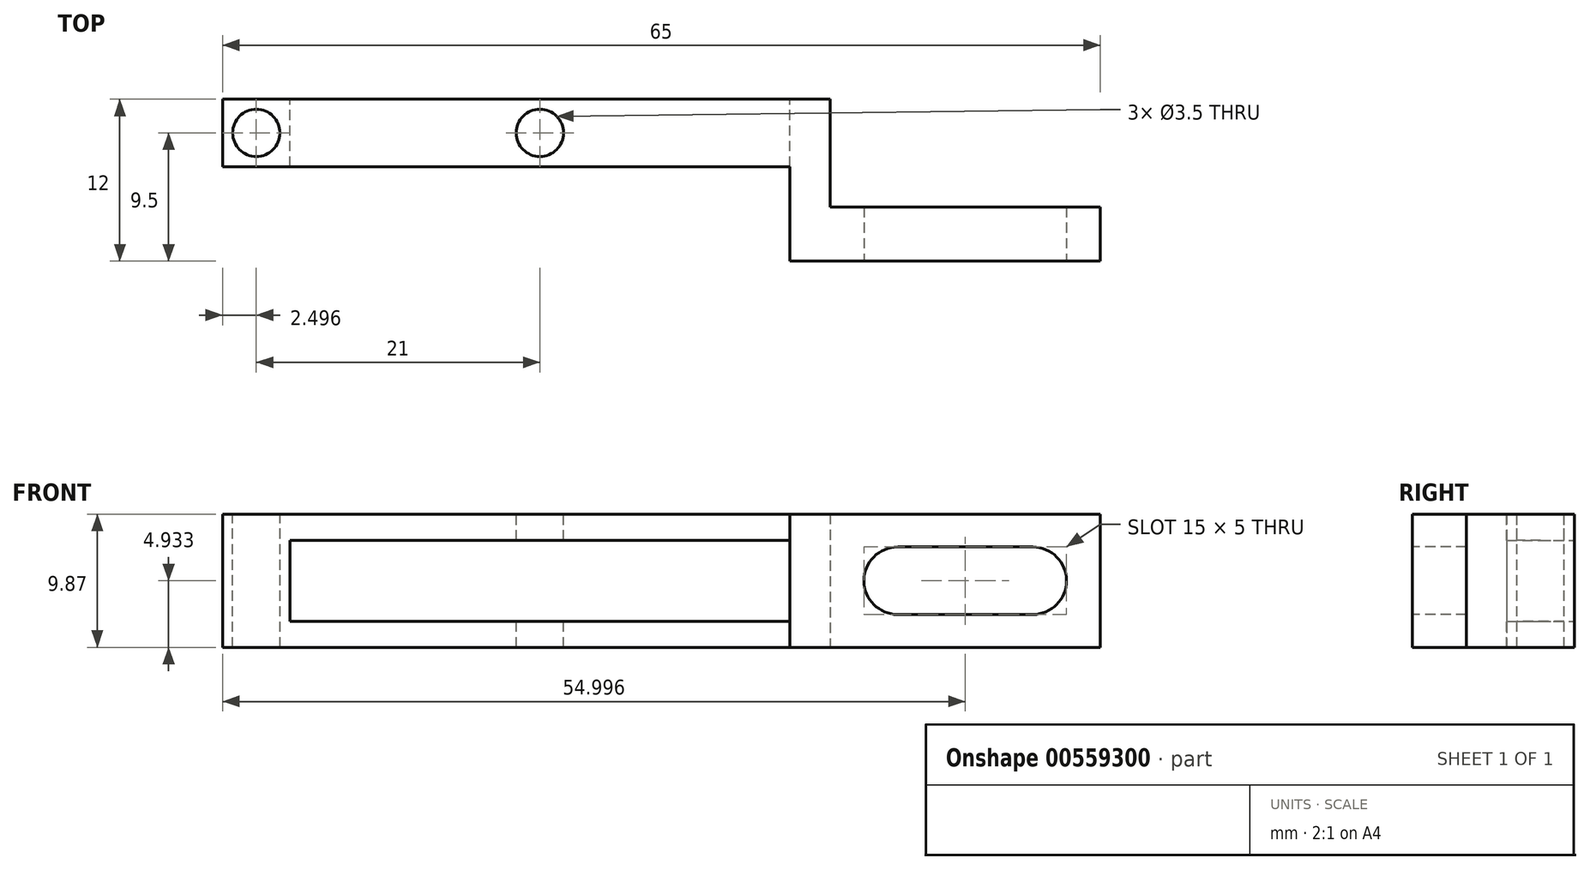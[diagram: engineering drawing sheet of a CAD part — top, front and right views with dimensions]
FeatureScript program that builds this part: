
annotation { "Feature Type Name" : "Feature", "Feature Type Description" : "" }
export const myFeature = defineFeature(function(context is Context, id is Id, definition is map)
    precondition{}
    {
        {
            var Q0;
            Q0=qCreatedBy(makeId("Front.planeOp"),FACE);
            var sketch = newSketch(context, id + "F0", { "sketchPlane" : qUnion([Q0])});
            skLineSegment(sketch, "E0.top", {"start": v(-18.46, -6.81) * mm, "end": v(26.54, -6.81) * mm});
            skLineSegment(sketch, "E0.left", {"start": v(-18.46, 3.06) * mm, "end": v(-18.46, -6.81) * mm});
            skLineSegment(sketch, "E1", {"start": v(-18.46, -1.88) * mm, "end": v(-1.71, -1.88) * mm, "construction": true});
            skLineSegment(sketch, "E2", {"start": v(-1.71, -1.88) * mm, "end": v(-1.71, -4.88) * mm, "construction": true});
            skLineSegment(sketch, "E3", {"start": v(-13.46, -4.88) * mm, "end": v(26.54, -4.88) * mm});
            skLineSegment(sketch, "E4", {"start": v(26.54, -4.88) * mm, "end": v(26.54, -6.81) * mm});
            skLineSegment(sketch, "E5", {"start": v(-18.46, 3.06) * mm, "end": v(26.54, 3.06) * mm});
            skLineSegment(sketch, "E6", {"start": v(-1.71, -1.88) * mm, "end": v(-1.71, 1.12) * mm});
            skLineSegment(sketch, "E7", {"start": v(26.54, 3.06) * mm, "end": v(26.54, 1.12) * mm});
            skLineSegment(sketch, "E8", {"start": v(26.54, 1.12) * mm, "end": v(-13.46, 1.12) * mm});
            skLineSegment(sketch, "E9", {"start": v(-13.46, 1.12) * mm, "end": v(-13.46, -4.88) * mm});
            skLineSegment(sketch, "E10", {"start": v(-13.46, -4.88) * mm, "end": v(-18.46, -4.88) * mm});
            skLineSegment(sketch, "E11", {"start": v(26.54, -4.88) * mm, "end": v(26.54, 1.12) * mm});
            skLineSegment(sketch, "E12", {"start": v(23.54, -4.88) * mm, "end": v(23.54, 1.12) * mm});
            skLineSegment(sketch, "E13", {"start": v(23.54, 1.12) * mm, "end": v(23.54, -1.88) * mm});
            skLineSegment(sketch, "E14", {"start": v(23.54, -1.88) * mm, "end": v(26.54, -1.88) * mm});
            skSolve(sketch);
        }
        {
            var Q0;
            Q0 = qSketchRegion(id + "F0", true);
            extrude(context, id + "F1", {"entities" : qUnion([Q0]), "depth" : 5 * mm, "offsetDistance" : 25 * mm});
        }
        {
            var Q0;
            Q0=makeQuery(id+"F1.opExtrude","SWEPT_FACE",FACE,{"disambiguationData":[OSD([sQuery(id+"F0.wireOp",EDGE,"E5")])]});
            var sketch = newSketch(context, id + "F2", { "sketchPlane" : qUnion([Q0])});
            skLineSegment(sketch, "E15", {"start": v(-18.46, 0) * mm, "end": v(-18.46, -5) * mm});
            skLineSegment(sketch, "E16", {"start": v(-18.46, -2.5) * mm, "end": v(-15.96, -2.5) * mm});
            skCircle(sketch, "E17", {"center": v(-15.96, -2.5) * mm, "radius": 1.75 * mm});
            skLineSegment(sketch, "E18", {"start": v(4.04, 0) * mm, "end": v(4.04, -2.5) * mm});
            skLineSegment(sketch, "E19", {"start": v(4.04, -2.5) * mm, "end": v(5.04, -2.5) * mm});
            skCircle(sketch, "E20", {"center": v(5.04, -2.5) * mm, "radius": 1.75 * mm});
            skCircle(sketch, "E21", {"center": v(5.04, -2.5) * mm, "radius": 10 * mm});
            skSolve(sketch);
        }
        {
            var Q0;
            Q0=makeQuery(id+"F2.imprint","IMPRINT",FACE,{"disambiguationData":[TD([[makeQuery(id+"F2.imprint","IMPRINT",EDGE,{"derivedFrom":sQuery(id+"F2.wireOp",EDGE,"E17")}),1.0]])]});
            var Q1;
            Q1=makeQuery(id+"F2.imprint","IMPRINT",FACE,{"disambiguationData":[TD([[makeQuery(id+"F2.imprint","IMPRINT",EDGE,{"derivedFrom":sQuery(id+"F2.wireOp",EDGE,"E20")}),1.0]])]});
            extrude(context, id + "F3", {"entities" : qUnion([Q0, Q1]), "operationType" : NewBodyOperationType.REMOVE, "oppositeDirection" : true, "depth" : 25 * mm, "offsetDistance" : 25 * mm});
        }
        {
            var Q0;
            Q0=makeQuery(id+"F1.opExtrude","CAP_FACE",FACE,{"disambiguationData":[OSD([sQuery(id+"F0.wireOp",EDGE,"E0.top"),sQuery(id+"F0.wireOp",EDGE,"E0.left"),sQuery(id+"F0.wireOp",EDGE,"E3"),sQuery(id+"F0.wireOp",EDGE,"E4"),sQuery(id+"F0.wireOp",EDGE,"E5"),sQuery(id+"F0.wireOp",EDGE,"E7"),sQuery(id+"F0.wireOp",EDGE,"E8"),sQuery(id+"F0.wireOp",EDGE,"E9"),sQuery(id+"F0.wireOp",EDGE,"E11"),sQuery(id+"F0.wireOp",EDGE,"E12")])],"isStart":false});
            var sketch = newSketch(context, id + "F4", { "sketchPlane" : qUnion([Q0])});
            skLineSegment(sketch, "E22", {"start": v(26.54, 3.06) * mm, "end": v(26.54, -6.81) * mm});
            skLineSegment(sketch, "E23", {"start": v(26.54, -6.81) * mm, "end": v(23.54, -6.81) * mm});
            skLineSegment(sketch, "E24", {"start": v(23.54, -6.81) * mm, "end": v(23.54, 3.06) * mm});
            skLineSegment(sketch, "E25", {"start": v(23.54, 3.06) * mm, "end": v(26.54, 3.06) * mm});
            skSolve(sketch);
        }
        {
            var Q0;
            Q0 = qSketchRegion(id + "F4", true);
            extrude(context, id + "F5", {"entities" : qUnion([Q0]), "operationType" : NewBodyOperationType.ADD, "depth" : 7 * mm, "offsetDistance" : 25 * mm});
        }
        {
            var Q0;
            Q0=makeQuery(id+"F5.boolean.opBoolean","MERGE",FACE,{"derivedFrom":[makeQuery(id+"F1.opExtrude","SWEPT_FACE",FACE,{"disambiguationData":[OSD([sQuery(id+"F0.wireOp",EDGE,"E4"),sQuery(id+"F0.wireOp",EDGE,"E7"),sQuery(id+"F0.wireOp",EDGE,"E11")])]}),makeQuery(id+"F5.opExtrude","SWEPT_FACE",FACE,{"disambiguationData":[OSD([sQuery(id+"F4.wireOp",EDGE,"E22")])]})]});
            var sketch = newSketch(context, id + "F6", { "sketchPlane" : qUnion([Q0])});
            skLineSegment(sketch, "E26", {"start": v(-12, -6.81) * mm, "end": v(-12, 3.06) * mm});
            skLineSegment(sketch, "E27", {"start": v(-12, 3.06) * mm, "end": v(-8, 3.06) * mm});
            skLineSegment(sketch, "E28", {"start": v(-8, 3.06) * mm, "end": v(-8, -6.81) * mm});
            skLineSegment(sketch, "E29", {"start": v(-8, -6.81) * mm, "end": v(-12, -6.81) * mm});
            skSolve(sketch);
        }
        {
            var Q0;
            Q0 = qSketchRegion(id + "F6", true);
            extrude(context, id + "F7", {"entities" : qUnion([Q0]), "operationType" : NewBodyOperationType.ADD, "depth" : 20 * mm, "offsetDistance" : 25 * mm});
        }
        {
            var Q0;
            Q0=makeQuery(id+"F7.boolean.opBoolean","MERGE",FACE,{"derivedFrom":[makeQuery(id+"F5.opExtrude","CAP_FACE",FACE,{"disambiguationData":[OSD([sQuery(id+"F4.wireOp",EDGE,"E22"),sQuery(id+"F4.wireOp",EDGE,"E23"),sQuery(id+"F4.wireOp",EDGE,"E24"),sQuery(id+"F4.wireOp",EDGE,"E25")])],"isStart":false}),makeQuery(id+"F7.opExtrude","SWEPT_FACE",FACE,{"disambiguationData":[OSD([sQuery(id+"F6.wireOp",EDGE,"E26")])]})]});
            var sketch = newSketch(context, id + "F8", { "sketchPlane" : qUnion([Q0])});
            skLineSegment(sketch, "E30", {"start": v(46.54, 3.06) * mm, "end": v(23.54, 3.06) * mm});
            skLineSegment(sketch, "E31", {"start": v(23.54, 3.06) * mm, "end": v(23.54, -6.81) * mm});
            skLineSegment(sketch, "E32", {"start": v(23.54, -6.81) * mm, "end": v(46.54, -6.81) * mm});
            skLineSegment(sketch, "E33", {"start": v(23.54, -1.88) * mm, "end": v(26.54, -1.88) * mm});
            skLineSegment(sketch, "E34", {"start": v(26.54, -1.88) * mm, "end": v(31.54, -1.88) * mm});
            skLineSegment(sketch, "E35", {"start": v(31.54, -1.88) * mm, "end": v(41.54, -1.88) * mm});
            skLineSegment(sketch, "E36", {"start": v(41.54, -1.88) * mm, "end": v(46.54, -1.88) * mm});
            skArc(sketch, "E37.0.startCap", {"start": v(31.54, -4.38) * mm, "mid": v(29.04, -1.88) * mm, "end": v(31.54, 0.62) * mm});
            skArc(sketch, "E37.0.endCap", {"start": v(41.54, 0.62) * mm, "mid": v(44.04, -1.88) * mm, "end": v(41.54, -4.38) * mm});
            skLineSegment(sketch, "E37.0.left", {"start": v(31.54, 0.62) * mm, "end": v(41.54, 0.62) * mm});
            skLineSegment(sketch, "E37.0.right", {"start": v(31.54, -4.38) * mm, "end": v(41.54, -4.38) * mm});
            skSolve(sketch);
        }
        {
            var Q0;
            Q0 = qSketchRegion(id + "F8", true);
            extrude(context, id + "F9", {"entities" : qUnion([Q0]), "operationType" : NewBodyOperationType.REMOVE, "oppositeDirection" : true, "depth" : 25 * mm, "offsetDistance" : 25 * mm});
        }
    });
